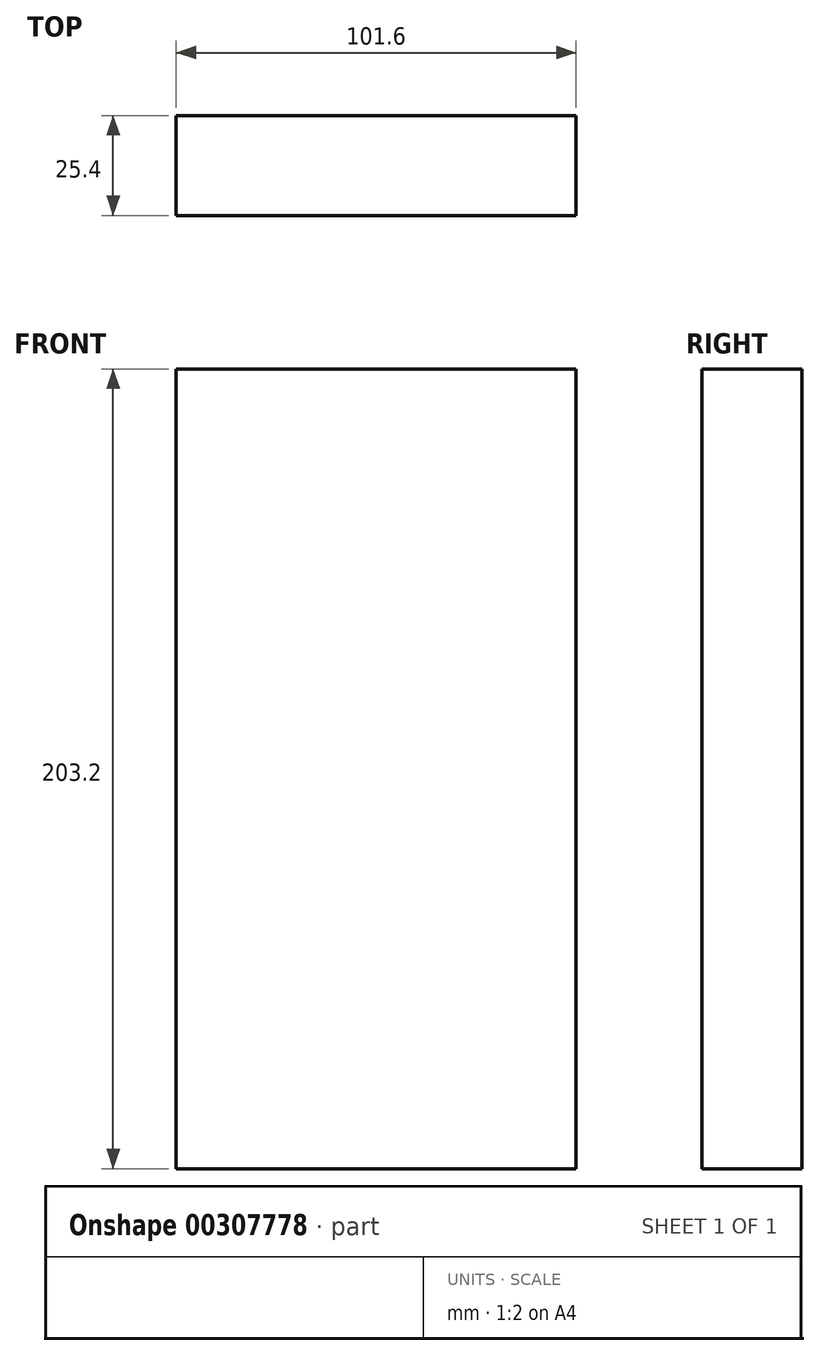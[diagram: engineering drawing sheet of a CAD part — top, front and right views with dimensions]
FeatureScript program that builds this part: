
annotation { "Feature Type Name" : "Feature", "Feature Type Description" : "" }
export const myFeature = defineFeature(function(context is Context, id is Id, definition is map)
    precondition{}
    {
        {
            var Q0;
            Q0=qCreatedBy(makeId("Front.planeOp"),FACE);
            var sketch = newSketch(context, id + "F0", { "sketchPlane" : qUnion([Q0])});
            skLineSegment(sketch, "E0.bottom", {"start": v(-64.03, 154.82) * mm, "end": v(37.57, 154.82) * mm});
            skLineSegment(sketch, "E0.top", {"start": v(-64.03, -48.38) * mm, "end": v(37.57, -48.38) * mm});
            skLineSegment(sketch, "E0.left", {"start": v(-64.03, 154.82) * mm, "end": v(-64.03, -48.38) * mm});
            skLineSegment(sketch, "E0.right", {"start": v(37.57, 154.82) * mm, "end": v(37.57, -48.38) * mm});
            skSolve(sketch);
        }
        {
            var Q0;
            Q0=makeQuery(id+"F0.imprint","IMPRINT",FACE,{"disambiguationData":[TD([[makeQuery(id+"F0.imprint","IMPRINT",EDGE,{"derivedFrom":sQuery(id+"F0.wireOp",EDGE,"E0.bottom")}),-1.0]])]});
            extrude(context, id + "F1", {"entities" : qUnion([Q0]), "depth" : 25.4 * mm});
        }
    });
